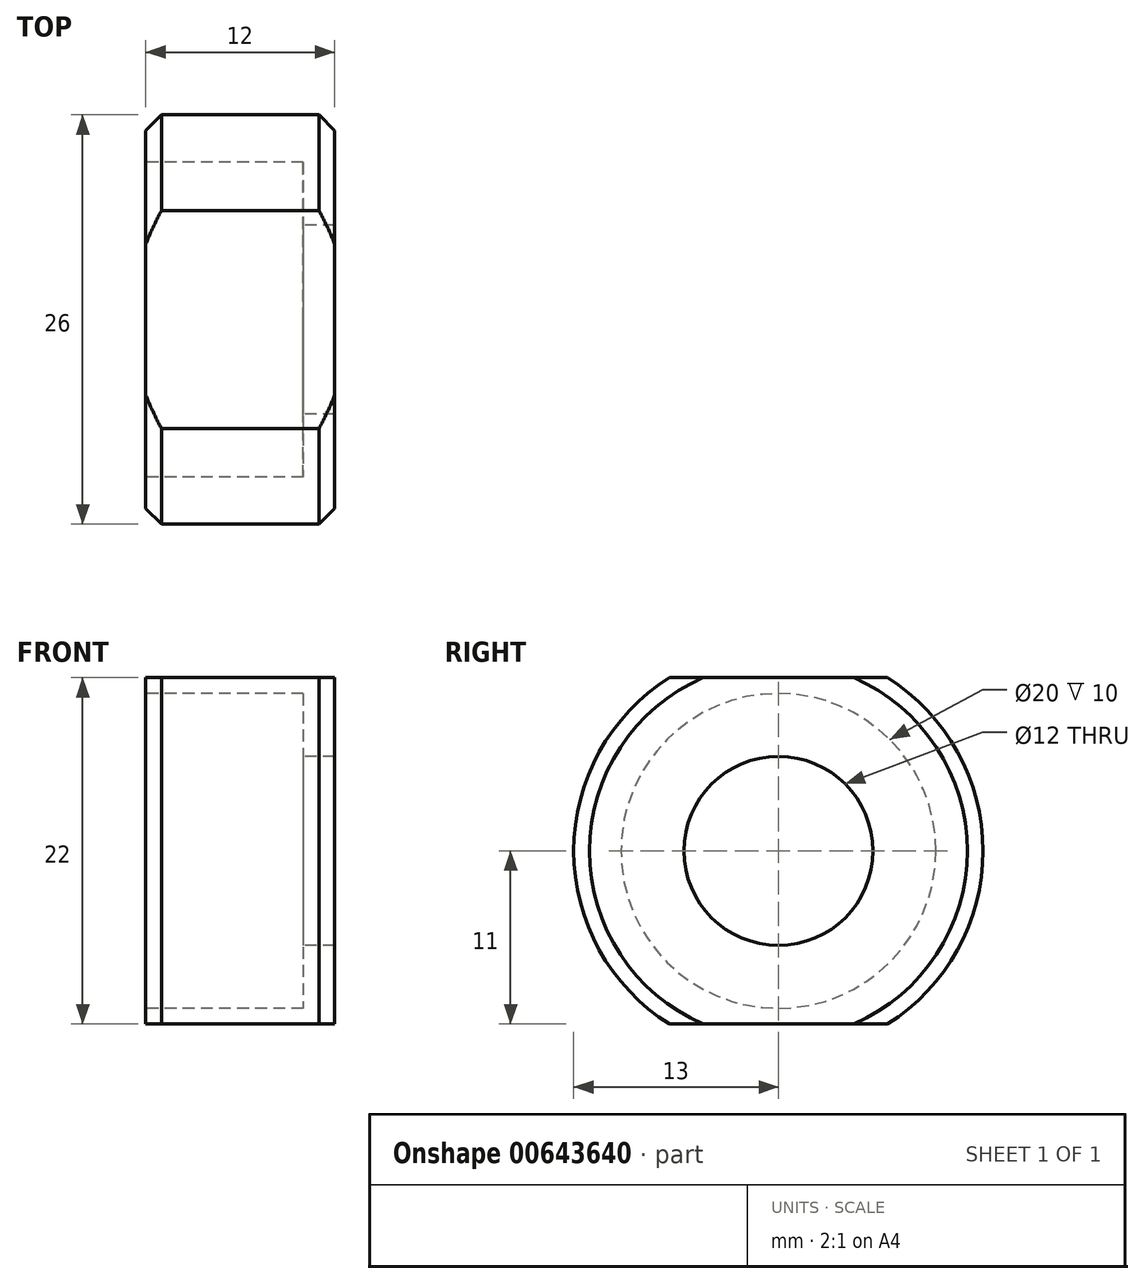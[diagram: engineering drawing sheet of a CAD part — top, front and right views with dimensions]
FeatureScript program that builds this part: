
annotation { "Feature Type Name" : "Feature", "Feature Type Description" : "" }
export const myFeature = defineFeature(function(context is Context, id is Id, definition is map)
    precondition{}
    {
        {
            var Q0;
            Q0=qCreatedBy(makeId("Front.planeOp"),FACE);
            var sketch = newSketch(context, id + "F0", { "sketchPlane" : qUnion([Q0])});
            skLineSegment(sketch, "E0", {"start": v(-12.14, 0) * mm, "end": v(12.57, 0) * mm, "construction": true});
            skLineSegment(sketch, "E1", {"start": v(0, 10) * mm, "end": v(0, 13) * mm});
            skLineSegment(sketch, "E2", {"start": v(0, 13) * mm, "end": v(12, 13) * mm});
            skLineSegment(sketch, "E3", {"start": v(12, 13) * mm, "end": v(12, 6) * mm});
            skLineSegment(sketch, "E4", {"start": v(12, 6) * mm, "end": v(10, 6) * mm});
            skLineSegment(sketch, "E5", {"start": v(10, 6) * mm, "end": v(10, 10) * mm});
            skLineSegment(sketch, "E6", {"start": v(10, 10) * mm, "end": v(0, 10) * mm});
            skSolve(sketch);
        }
        {
            var Q0;
            Q0 = qSketchRegion(id + "F0", true);
            var Q1;
            Q1=sQuery(id+"F0.wireOp",EDGE,"E0");
            revolve(context, id + "F1", {"entities" : qUnion([Q0]), "axis" : qUnion([Q1]), "revolveType" : RevolveType.FULL});
        }
        {
            var Q0;
            Q0=makeQuery(id+"F1.opRevolve","SWEPT_EDGE",EDGE,{"disambiguationData":[OSD([sQuery(id+"F0.wireOp",EDGE,"E2"),sQuery(id+"F0.wireOp",EDGE,"E3")])]});
            var Q1;
            Q1=makeQuery(id+"F1.opRevolve","SWEPT_EDGE",EDGE,{"disambiguationData":[OSD([sQuery(id+"F0.wireOp",EDGE,"E1"),sQuery(id+"F0.wireOp",EDGE,"E2")])]});
            chamfer(context, id + "F2", {"entities" : qUnion([Q0, Q1]), "width" : 1 * mm, "tangentPropagation" : true});
        }
        {
            var Q0;
            Q0=qCreatedBy(makeId("Front.planeOp"),FACE);
            var sketch = newSketch(context, id + "F3", { "sketchPlane" : qUnion([Q0])});
            skLineSegment(sketch, "E7.bottom", {"start": v(-0.57, 11) * mm, "end": v(14.77, 11) * mm});
            skLineSegment(sketch, "E7.top", {"start": v(-0.57, 15.75) * mm, "end": v(14.77, 15.75) * mm});
            skLineSegment(sketch, "E7.left", {"start": v(-0.57, 11) * mm, "end": v(-0.57, 15.75) * mm});
            skLineSegment(sketch, "E7.right", {"start": v(14.77, 11) * mm, "end": v(14.77, 15.75) * mm});
            skLineSegment(sketch, "E8.bottom", {"start": v(-0.44, -11) * mm, "end": v(14.87, -11) * mm});
            skLineSegment(sketch, "E8.top", {"start": v(-0.44, -18.73) * mm, "end": v(14.87, -18.73) * mm});
            skLineSegment(sketch, "E8.left", {"start": v(-0.44, -11) * mm, "end": v(-0.44, -18.73) * mm});
            skLineSegment(sketch, "E8.right", {"start": v(14.87, -11) * mm, "end": v(14.87, -18.73) * mm});
            skSolve(sketch);
        }
        {
            var Q0;
            Q0 = qSketchRegion(id + "F3", true);
            extrude(context, id + "F4", {"entities" : qUnion([Q0]), "operationType" : NewBodyOperationType.REMOVE, "depth" : 25 * mm, "offsetDistance" : 25 * mm, "symmetric" : true});
        }
    });
